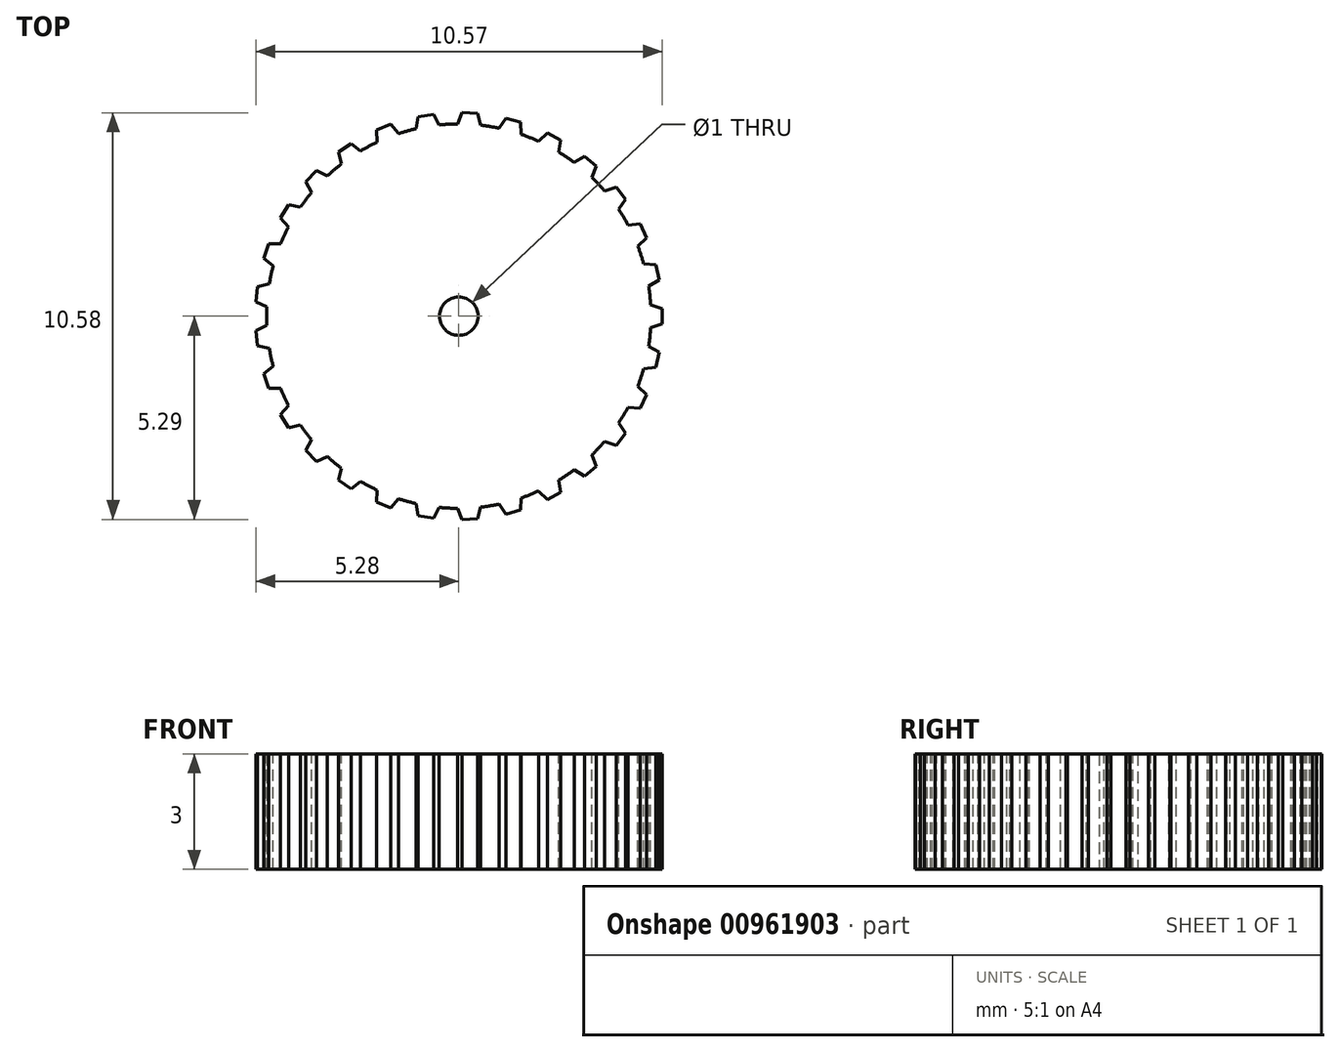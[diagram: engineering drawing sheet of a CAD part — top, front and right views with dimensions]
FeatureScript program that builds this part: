
annotation { "Feature Type Name" : "Feature", "Feature Type Description" : "" }
export const myFeature = defineFeature(function(context is Context, id is Id, definition is map)
    precondition{}
    {
        {
            assignVariable(context, id + "F0", {"name" : "ID", "anyValue" : 10});
        }
        {
            assignVariable(context, id + "F1", {"name" : "IW", "anyValue" : 0.6});
        }
        {
            assignVariable(context, id + "F2", {"name" : "GD", "anyValue" : 3});
        }
        {
            var Q0;
            Q0=qCreatedBy(makeId("Top.planeOp"),FACE);
            var sketch = newSketch(context, id + "F3", { "sketchPlane" : qUnion([Q0])});
            skCircle(sketch, "E0", {"center": v(0, 0) * mm, "radius": 5 * mm});
            skSolve(sketch);
        }
        {
            var Q0;
            Q0=qSketchRegion(id+"F3",true);
            extrude(context, id + "F4", {"entities" : qUnion([Q0]), "depth" : (getVariable(context, 'GD')) * mm, "offsetDistance" : 25 * mm});
        }
        {
            var Q0;
            Q0=makeQuery(id+"F4.opExtrude","CAP_FACE",FACE,{"disambiguationData":[OSD([sQuery(id+"F3.wireOp",EDGE,"E0")])],"isStart":false});
            var sketch = newSketch(context, id + "F5", { "sketchPlane" : qUnion([Q0])});
            skLineSegment(sketch, "E1", {"start": v(0, 0) * mm, "end": v(14.18, 0) * mm, "construction": true});
            skLineSegment(sketch, "E2", {"start": v(5.3, 0.2) * mm, "end": v(5.3, -0.2) * mm});
            skLineSegment(sketch, "E3", {"start": v(5.3, -0.2) * mm, "end": v(5, -0.3) * mm});
            skLineSegment(sketch, "E4", {"start": v(5, -0.3) * mm, "end": v(5, 0.3) * mm, "construction": true});
            skLineSegment(sketch, "E5", {"start": v(5, 0.3) * mm, "end": v(5.3, 0.2) * mm});
            skLineSegment(sketch, "E6", {"start": v(5, 0.3) * mm, "end": v(4.9, 0.3) * mm});
            skLineSegment(sketch, "E7", {"start": v(4.9, 0.3) * mm, "end": v(4.9, -0.3) * mm});
            skLineSegment(sketch, "E8", {"start": v(4.9, -0.3) * mm, "end": v(5, -0.3) * mm});
            skSolve(sketch);
        }
        {
            assignVariable(context, id + "F6", {"name" : "TM1", "anyValue" : 3.14 * 2 * getVariable(context, 'ID')});
        }
        {
            assignVariable(context, id + "F7", {"name" : "NoT", "anyValue" : floor((getVariable(context, 'TM1')) / (3.5 * getVariable(context, 'IW')))});
        }
        {
            var Q0;
            Q0=qSketchRegion(id+"F5",true);
            extrude(context, id + "F8", {"entities" : qUnion([Q0]), "oppositeDirection" : true, "depth" : (getVariable(context, 'GD')) * mm, "offsetDistance" : 25 * mm});
        }
        {
            var Q0;
            Q0=makeQuery(id+"F8.opExtrude","SWEPT_BODY",BODY,{"disambiguationData":[OSD([sQuery(id+"F5.wireOp",EDGE,"E2"),sQuery(id+"F5.wireOp",EDGE,"E3"),sQuery(id+"F5.wireOp",EDGE,"E5"),sQuery(id+"F5.wireOp",EDGE,"E6"),sQuery(id+"F5.wireOp",EDGE,"E7"),sQuery(id+"F5.wireOp",EDGE,"E8")])]});
            var Q1;
            Q1=makeQuery(id+"F4.opExtrude","SWEPT_FACE",FACE,{"disambiguationData":[OSD([sQuery(id+"F3.wireOp",EDGE,"E0")])]});
            circularPattern(context, id + "F9", {"operationType" : NewBodyOperationType.ADD, "entities" : qUnion([Q0]), "axis" : qUnion([Q1]), "angle" : 360 * degree, "instanceCount" : getVariable(context, 'NoT'), "equalSpace" : true});
        }
        {
            var Q0;
            {var subQ0=makeQuery(id+"F8.opExtrude","CAP_FACE",FACE,{"disambiguationData":[OSD([sQuery(id+"F5.wireOp",EDGE,"E2"),sQuery(id+"F5.wireOp",EDGE,"E3"),sQuery(id+"F5.wireOp",EDGE,"E5"),sQuery(id+"F5.wireOp",EDGE,"E6"),sQuery(id+"F5.wireOp",EDGE,"E7"),sQuery(id+"F5.wireOp",EDGE,"E8")])],"isStart":false});Q0=makeQuery(id+"F9.boolean.opBoolean","MERGE",FACE,{"derivedFrom":[makeQuery(id+"F4.opExtrude","CAP_FACE",FACE,{"disambiguationData":[OSD([sQuery(id+"F3.wireOp",EDGE,"E0")])],"isStart":true}),subQ0,makeQuery(id+"F9.opPattern","COPY",FACE,{"derivedFrom":subQ0,"instanceName":"1"}),makeQuery(id+"F9.opPattern","COPY",FACE,{"derivedFrom":subQ0,"instanceName":"2"}),makeQuery(id+"F9.opPattern","COPY",FACE,{"derivedFrom":subQ0,"instanceName":"3"}),makeQuery(id+"F9.opPattern","COPY",FACE,{"derivedFrom":subQ0,"instanceName":"4"}),makeQuery(id+"F9.opPattern","COPY",FACE,{"derivedFrom":subQ0,"instanceName":"5"}),makeQuery(id+"F9.opPattern","COPY",FACE,{"derivedFrom":subQ0,"instanceName":"6"}),makeQuery(id+"F9.opPattern","COPY",FACE,{"derivedFrom":subQ0,"instanceName":"7"}),makeQuery(id+"F9.opPattern","COPY",FACE,{"derivedFrom":subQ0,"instanceName":"8"}),makeQuery(id+"F9.opPattern","COPY",FACE,{"derivedFrom":subQ0,"instanceName":"9"}),makeQuery(id+"F9.opPattern","COPY",FACE,{"derivedFrom":subQ0,"instanceName":"10"}),makeQuery(id+"F9.opPattern","COPY",FACE,{"derivedFrom":subQ0,"instanceName":"11"}),makeQuery(id+"F9.opPattern","COPY",FACE,{"derivedFrom":subQ0,"instanceName":"12"}),makeQuery(id+"F9.opPattern","COPY",FACE,{"derivedFrom":subQ0,"instanceName":"13"}),makeQuery(id+"F9.opPattern","COPY",FACE,{"derivedFrom":subQ0,"instanceName":"14"}),makeQuery(id+"F9.opPattern","COPY",FACE,{"derivedFrom":subQ0,"instanceName":"15"}),makeQuery(id+"F9.opPattern","COPY",FACE,{"derivedFrom":subQ0,"instanceName":"16"}),makeQuery(id+"F9.opPattern","COPY",FACE,{"derivedFrom":subQ0,"instanceName":"17"}),makeQuery(id+"F9.opPattern","COPY",FACE,{"derivedFrom":subQ0,"instanceName":"18"}),makeQuery(id+"F9.opPattern","COPY",FACE,{"derivedFrom":subQ0,"instanceName":"19"}),makeQuery(id+"F9.opPattern","COPY",FACE,{"derivedFrom":subQ0,"instanceName":"20"}),makeQuery(id+"F9.opPattern","COPY",FACE,{"derivedFrom":subQ0,"instanceName":"21"}),makeQuery(id+"F9.opPattern","COPY",FACE,{"derivedFrom":subQ0,"instanceName":"22"}),makeQuery(id+"F9.opPattern","COPY",FACE,{"derivedFrom":subQ0,"instanceName":"23"}),makeQuery(id+"F9.opPattern","COPY",FACE,{"derivedFrom":subQ0,"instanceName":"24"}),makeQuery(id+"F9.opPattern","COPY",FACE,{"derivedFrom":subQ0,"instanceName":"25"}),makeQuery(id+"F9.opPattern","COPY",FACE,{"derivedFrom":subQ0,"instanceName":"26"}),makeQuery(id+"F9.opPattern","COPY",FACE,{"derivedFrom":subQ0,"instanceName":"27"}),makeQuery(id+"F9.opPattern","COPY",FACE,{"derivedFrom":subQ0,"instanceName":"28"}),makeQuery(id+"F9.opPattern","COPY",FACE,{"derivedFrom":subQ0,"instanceName":"29"}),makeQuery(id+"F9.opPattern","COPY",FACE,{"derivedFrom":subQ0,"instanceName":"30"}),makeQuery(id+"F9.opPattern","COPY",FACE,{"derivedFrom":subQ0,"instanceName":"31"}),makeQuery(id+"F9.opPattern","COPY",FACE,{"derivedFrom":subQ0,"instanceName":"32"}),makeQuery(id+"F9.opPattern","COPY",FACE,{"derivedFrom":subQ0,"instanceName":"33"}),makeQuery(id+"F9.opPattern","COPY",FACE,{"derivedFrom":subQ0,"instanceName":"34"}),makeQuery(id+"F9.opPattern","COPY",FACE,{"derivedFrom":subQ0,"instanceName":"35"}),makeQuery(id+"F9.opPattern","COPY",FACE,{"derivedFrom":subQ0,"instanceName":"36"}),makeQuery(id+"F9.opPattern","COPY",FACE,{"derivedFrom":subQ0,"instanceName":"37"}),makeQuery(id+"F9.opPattern","COPY",FACE,{"derivedFrom":subQ0,"instanceName":"38"}),makeQuery(id+"F9.opPattern","COPY",FACE,{"derivedFrom":subQ0,"instanceName":"39"}),makeQuery(id+"F9.opPattern","COPY",FACE,{"derivedFrom":subQ0,"instanceName":"40"}),makeQuery(id+"F9.opPattern","COPY",FACE,{"derivedFrom":subQ0,"instanceName":"41"}),makeQuery(id+"F9.opPattern","COPY",FACE,{"derivedFrom":subQ0,"instanceName":"42"}),makeQuery(id+"F9.opPattern","COPY",FACE,{"derivedFrom":subQ0,"instanceName":"43"})]});}
            var sketch = newSketch(context, id + "F10", { "sketchPlane" : qUnion([Q0])});
            skCircle(sketch, "E9", {"center": v(0, 0) * mm, "radius": 0.5 * mm});
            skSolve(sketch);
        }
        {
            var Q0;
            Q0=makeQuery(id+"F10.imprint","IMPRINT",FACE,{"disambiguationData":[TD([[makeQuery(id+"F10.imprint","IMPRINT",EDGE,{"derivedFrom":sQuery(id+"F10.wireOp",EDGE,"E9")}),1.0]])]});
            var Q1;
            {var subQ0=makeQuery(id+"F8.opExtrude","CAP_FACE",FACE,{"disambiguationData":[OSD([sQuery(id+"F5.wireOp",EDGE,"E2"),sQuery(id+"F5.wireOp",EDGE,"E3"),sQuery(id+"F5.wireOp",EDGE,"E5"),sQuery(id+"F5.wireOp",EDGE,"E6"),sQuery(id+"F5.wireOp",EDGE,"E7"),sQuery(id+"F5.wireOp",EDGE,"E8")])],"isStart":true});Q1=makeQuery(id+"F9.boolean.opBoolean","MERGE",FACE,{"derivedFrom":[makeQuery(id+"F4.opExtrude","CAP_FACE",FACE,{"disambiguationData":[OSD([sQuery(id+"F3.wireOp",EDGE,"E0")])],"isStart":false}),subQ0,makeQuery(id+"F9.opPattern","COPY",FACE,{"derivedFrom":subQ0,"instanceName":"1"}),makeQuery(id+"F9.opPattern","COPY",FACE,{"derivedFrom":subQ0,"instanceName":"2"}),makeQuery(id+"F9.opPattern","COPY",FACE,{"derivedFrom":subQ0,"instanceName":"3"}),makeQuery(id+"F9.opPattern","COPY",FACE,{"derivedFrom":subQ0,"instanceName":"4"}),makeQuery(id+"F9.opPattern","COPY",FACE,{"derivedFrom":subQ0,"instanceName":"5"}),makeQuery(id+"F9.opPattern","COPY",FACE,{"derivedFrom":subQ0,"instanceName":"6"}),makeQuery(id+"F9.opPattern","COPY",FACE,{"derivedFrom":subQ0,"instanceName":"7"}),makeQuery(id+"F9.opPattern","COPY",FACE,{"derivedFrom":subQ0,"instanceName":"8"}),makeQuery(id+"F9.opPattern","COPY",FACE,{"derivedFrom":subQ0,"instanceName":"9"}),makeQuery(id+"F9.opPattern","COPY",FACE,{"derivedFrom":subQ0,"instanceName":"10"}),makeQuery(id+"F9.opPattern","COPY",FACE,{"derivedFrom":subQ0,"instanceName":"11"}),makeQuery(id+"F9.opPattern","COPY",FACE,{"derivedFrom":subQ0,"instanceName":"12"}),makeQuery(id+"F9.opPattern","COPY",FACE,{"derivedFrom":subQ0,"instanceName":"13"}),makeQuery(id+"F9.opPattern","COPY",FACE,{"derivedFrom":subQ0,"instanceName":"14"}),makeQuery(id+"F9.opPattern","COPY",FACE,{"derivedFrom":subQ0,"instanceName":"15"}),makeQuery(id+"F9.opPattern","COPY",FACE,{"derivedFrom":subQ0,"instanceName":"16"}),makeQuery(id+"F9.opPattern","COPY",FACE,{"derivedFrom":subQ0,"instanceName":"17"}),makeQuery(id+"F9.opPattern","COPY",FACE,{"derivedFrom":subQ0,"instanceName":"18"}),makeQuery(id+"F9.opPattern","COPY",FACE,{"derivedFrom":subQ0,"instanceName":"19"}),makeQuery(id+"F9.opPattern","COPY",FACE,{"derivedFrom":subQ0,"instanceName":"20"}),makeQuery(id+"F9.opPattern","COPY",FACE,{"derivedFrom":subQ0,"instanceName":"21"}),makeQuery(id+"F9.opPattern","COPY",FACE,{"derivedFrom":subQ0,"instanceName":"22"}),makeQuery(id+"F9.opPattern","COPY",FACE,{"derivedFrom":subQ0,"instanceName":"23"}),makeQuery(id+"F9.opPattern","COPY",FACE,{"derivedFrom":subQ0,"instanceName":"24"}),makeQuery(id+"F9.opPattern","COPY",FACE,{"derivedFrom":subQ0,"instanceName":"25"}),makeQuery(id+"F9.opPattern","COPY",FACE,{"derivedFrom":subQ0,"instanceName":"26"}),makeQuery(id+"F9.opPattern","COPY",FACE,{"derivedFrom":subQ0,"instanceName":"27"}),makeQuery(id+"F9.opPattern","COPY",FACE,{"derivedFrom":subQ0,"instanceName":"28"}),makeQuery(id+"F9.opPattern","COPY",FACE,{"derivedFrom":subQ0,"instanceName":"29"}),makeQuery(id+"F9.opPattern","COPY",FACE,{"derivedFrom":subQ0,"instanceName":"30"}),makeQuery(id+"F9.opPattern","COPY",FACE,{"derivedFrom":subQ0,"instanceName":"31"}),makeQuery(id+"F9.opPattern","COPY",FACE,{"derivedFrom":subQ0,"instanceName":"32"}),makeQuery(id+"F9.opPattern","COPY",FACE,{"derivedFrom":subQ0,"instanceName":"33"}),makeQuery(id+"F9.opPattern","COPY",FACE,{"derivedFrom":subQ0,"instanceName":"34"}),makeQuery(id+"F9.opPattern","COPY",FACE,{"derivedFrom":subQ0,"instanceName":"35"}),makeQuery(id+"F9.opPattern","COPY",FACE,{"derivedFrom":subQ0,"instanceName":"36"}),makeQuery(id+"F9.opPattern","COPY",FACE,{"derivedFrom":subQ0,"instanceName":"37"}),makeQuery(id+"F9.opPattern","COPY",FACE,{"derivedFrom":subQ0,"instanceName":"38"}),makeQuery(id+"F9.opPattern","COPY",FACE,{"derivedFrom":subQ0,"instanceName":"39"}),makeQuery(id+"F9.opPattern","COPY",FACE,{"derivedFrom":subQ0,"instanceName":"40"}),makeQuery(id+"F9.opPattern","COPY",FACE,{"derivedFrom":subQ0,"instanceName":"41"}),makeQuery(id+"F9.opPattern","COPY",FACE,{"derivedFrom":subQ0,"instanceName":"42"}),makeQuery(id+"F9.opPattern","COPY",FACE,{"derivedFrom":subQ0,"instanceName":"43"})]});}
            extrude(context, id + "F11", {"entities" : qUnion([Q0]), "operationType" : NewBodyOperationType.REMOVE, "endBound" : BoundingType.UP_TO_SURFACE, "oppositeDirection" : true, "depth" : 25 * mm, "endBoundEntityFace" : qUnion([Q1]), "offsetDistance" : 25 * mm});
        }
    });
